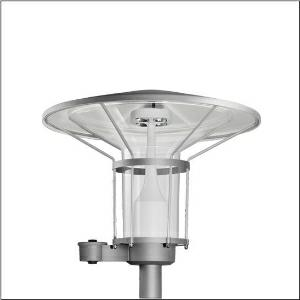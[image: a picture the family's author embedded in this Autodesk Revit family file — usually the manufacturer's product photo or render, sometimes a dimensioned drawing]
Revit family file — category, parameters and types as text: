
# Revit family: laterne_classic_iq___st1_2a_5xa5245eu14h000022_d57d
name_source: partatom
category: Lighting Fixtures
units: mm (PartAtom-declared; Revit-internal decimal feet)

## family parameters
Cut with Voids When Loaded = No
Host = Face
Light Source = No
Part Type = Normal
Room Calculation Point = No
Round Connector Dimension = Use Diameter
Shared = No

## types (1)
- --- (1 x LED, 1370 lm, 10.7 W, 3000K)
    Apparent Load = 11 VA
    CIE Flux Codes = 21 60 93 97 100
    Color Rendering = 70
    Color Temperature = 3000K
    Default Elevation = 1800 mm
    Description = Lantern Classic iQ, mast luminaire, Module 540 iQ-SR, primary light control with 3 zone facetted reflector, of plastic, silver coated, highly specular, structured, primary optical cover: cover, of PMMA, transparent, light distribution: ST1.2a, light emission: direct distribution, primary light characteristic: asymmetric, installation type: post-top, LED, High Power LED, rated luminous flux: 1.370lm, luminous efficacy: 128lm/W, light colour: 730, colour temperature: 3000K, control gear: iQ-Street Remote, D4i with power reduction, control: optimised constant luminous flux control (CLO 2.0), Desk-Remote (wireless, voltage-free reading and setting of iQ features in the workshop via application-optimized NFC function/RFID function), Light-Fading, Smart-Wire, Night-Set, Lumen-Switch, Temp-Guard, Auto-Match, Street-Remote, pre-setting: logarithmic dimming characteristic, with terminal, 6-pole, max. 2.5mm², mains connection: 230..240V, AC, 50/60Hz, connection cable pre-assembled, cable length: 5,5m, wiring characteristics: H07RN-F, start of lifetime: 11W, end of service life: 11W, reduction: 6W, luminaire housing, upper part, of glass-fibre reinforced polyester, coated, Siteco® metallic grey (DB 702S), diameter: 750mm, height: 596mm, spigot size: d x l = 76 x 70mm (post-top) | with reducer (optional accessory) 60 x 70mm, mounting height: 3..5m, post-top mast mounting element, of diecast aluminium, coated, Siteco® metallic grey (DB 702S), Module 540 iQ-SR, traffic white (RAL 9016), equipment: standard, Smart Interface below, protection rating (complete): IP65, insulation class (complete): insulation class II (safety insulation), certification: CE, ENEC, VDE, packaging unit: 1 piece

Light Distribution: ST1.2a
    Height = 596 mm
    Lamp = 1 x LED
    Lamp Light Flux = 1370 lm
    Lamp Power = 10.7 W
    Lamp count = 1
    Length = 750 mm
    Luminous efficacy = 128 lm/W
    Manufacturer = Siteco
    ModVariant = No
    Model = 5XA5245EU14H000022
    Number of Poles = 1
    OnlyDefault = Yes
    Power Factor = 1
    Product Name = Laterne Classic iQ | ST1.2a
    Product group = mast luminaire | pylon top
    ProductGroupID = 6100
    Protection Class = Protection class II
    Protection Degree = IP 65
    RLX_Detail_Level = 1
    RLX_Emergency_Light_Flux = 0 lm
    RLX_Emergency_Type = 0
    RLX_Emergency_Type_DB = No
    RlxData = <blob elided: 63877 chars, md5=b591ae8d>
    Socket = socket
    Standby Power = 0 W
    System Light Flux = 1370 lm
    System Power = 11 W
    Type Comments = factory setting: luminous flux: 100 % | dim-lin: 254 | 419 mA
    Type Image = l_1006522.jpg
    URL = http://relux.com
    VarID = @adj_108157
    Voltage = 0 V
    Weight = 0.00 kg
    Width = 0 mm  [stored 0 ft]

note: [stored X ft] marks values corroborated as IEEE doubles in the binary element streams (Revit-internal decimal feet)

## geometry (parser evidence)
native form markers: Blend x4, Sweep x9
no freeform markers — native parametric forms only
